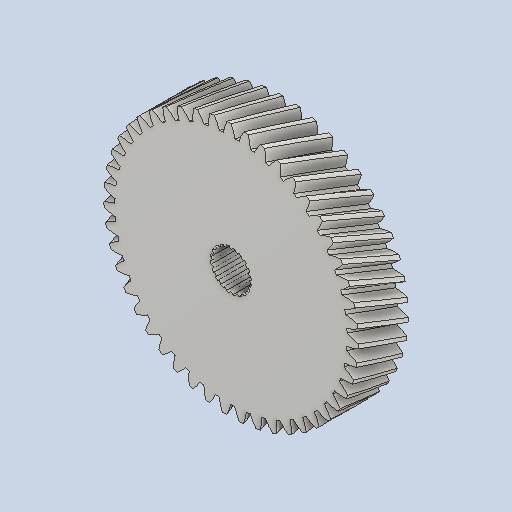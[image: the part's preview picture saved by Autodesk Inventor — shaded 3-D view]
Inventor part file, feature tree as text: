
AUTODESK INVENTOR PART (.ipt)
format: ipt  version: 2025.1 (Build 291241020, 241B)  size: 762,368 bytes
history: native  units: mm (DEFAULTED — no unit token found)
features: plane x3, other x3, extrude x2, sketch x2
ambient origin geometry x8: Origin, YZ Plane, XZ Plane, XY Plane, X Axis, Y Axis, Z Axis, Center Point
bodies: Solid1 (feature_tree)
feature tree (10):
  extrude  "Extrusion1"  Depth=15.0mm TaperAngle=0.0deg
  plane  "Work Plane2"
  plane  "Work Plane8"
  plane  "Work Plane9"
  other  "Spur Gear"
  extrude  "Extrusion2"  Depth=10.0mm TaperAngle=0.0deg
  sketch  "Sketch1"  dims[d0=76.235534mm d1=15.0mm d2=0.0mm]
  other  "Srf1"
  sketch  "Sketch Circular Pattern1"  dims[d3=73.194666mm d4=10.0mm d5=0.0mm d16=63.909111mm d17=0.0mm d34=0.668424mm d39=0.0mm d41=0.0mm d43=63.909111mm d46=63.909111mm d47=0.0mm d48=0.0mm d49=12.217mm d50=0.0mm d51=0.0mm d52=6.1135mm d53=0.515mm d54=200.0mm d56=360.0deg]
  other  "Pitch Diameter"
